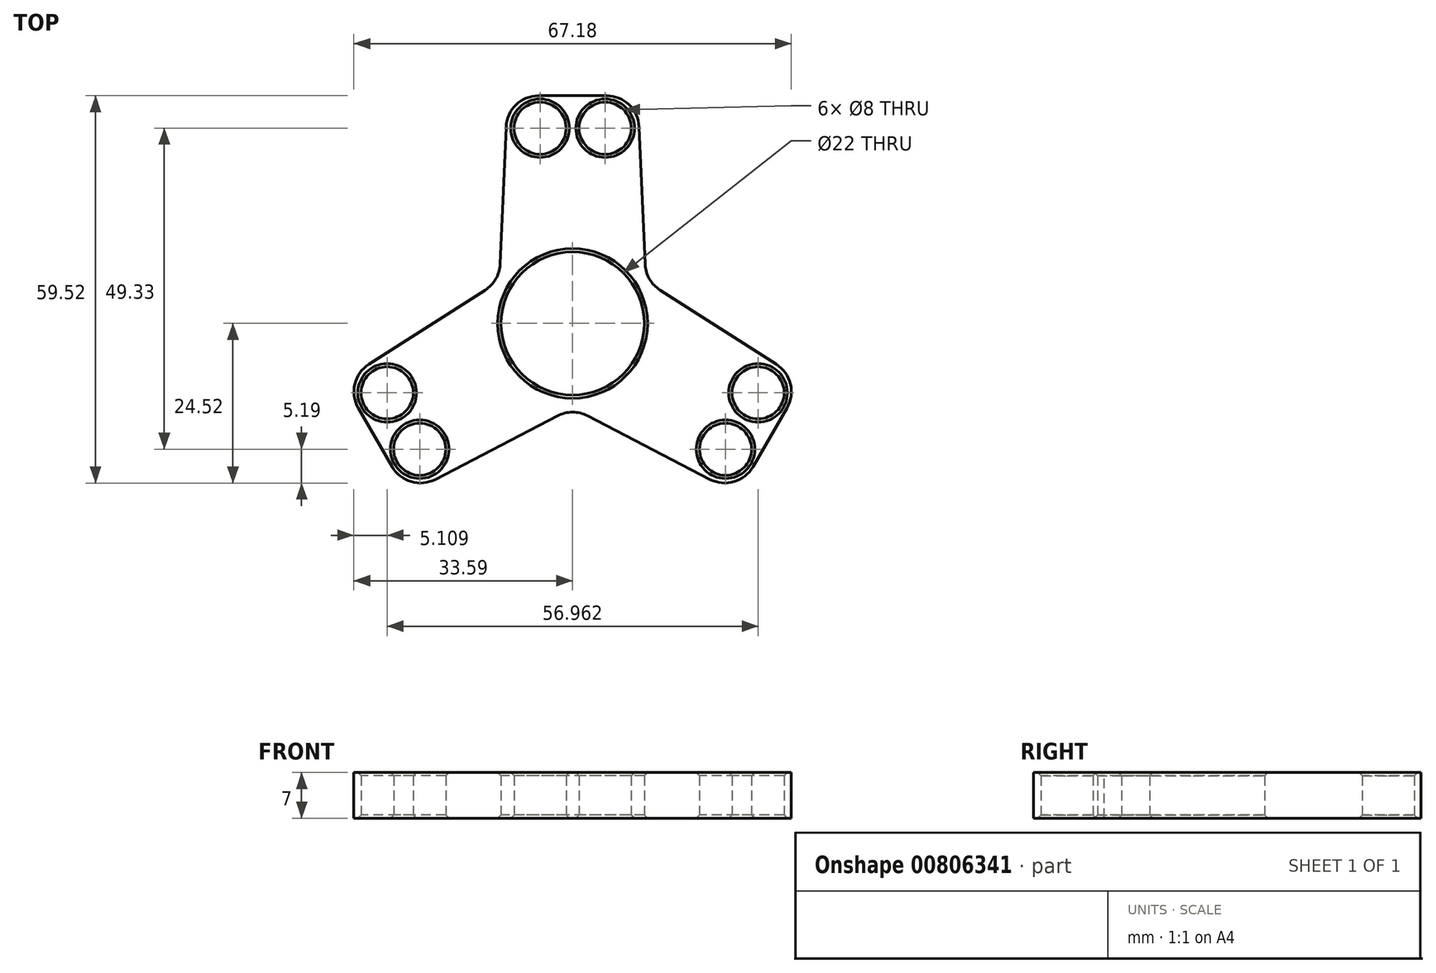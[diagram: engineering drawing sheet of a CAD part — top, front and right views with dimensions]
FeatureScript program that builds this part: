
annotation { "Feature Type Name" : "Feature", "Feature Type Description" : "" }
export const myFeature = defineFeature(function(context is Context, id is Id, definition is map)
    precondition{}
    {
        {
            var Q0;
            Q0=qCreatedBy(makeId("Top.planeOp"),FACE);
            var sketch = newSketch(context, id + "F0", { "sketchPlane" : qUnion([Q0])});
            skCircle(sketch, "E0", {"center": v(0, 0) * mm, "radius": 11 * mm});
            skCircle(sketch, "E1", {"center": v(0, 0) * mm, "radius": 13 * mm});
            skCircle(sketch, "E2", {"center": v(-5, 30) * mm, "radius": 4 * mm});
            skCircle(sketch, "E3.MirrorC", {"center": v(5, 30) * mm, "radius": 4 * mm});
            skCircle(sketch, "E4.1.0", {"center": v(-23.48, -19.33) * mm, "radius": 4 * mm});
            skCircle(sketch, "E4.1.1", {"center": v(-28.48, -10.67) * mm, "radius": 4 * mm});
            skCircle(sketch, "E4.2.0", {"center": v(28.48, -10.67) * mm, "radius": 4 * mm});
            skCircle(sketch, "E4.2.1", {"center": v(23.48, -19.33) * mm, "radius": 4 * mm});
            skLineSegment(sketch, "E5", {"start": v(0, 0) * mm, "end": v(-40.63, 23.46) * mm, "construction": true});
            skLineSegment(sketch, "E6", {"start": v(0, 0) * mm, "end": v(38.82, 22.41) * mm, "construction": true});
            skLineSegment(sketch, "E7", {"start": v(-11.26, 6.5) * mm, "end": v(-10, 35) * mm});
            skLineSegment(sketch, "E8", {"start": v(-10, 35) * mm, "end": v(10, 35) * mm});
            skLineSegment(sketch, "E9", {"start": v(10, 35) * mm, "end": v(11.26, 6.5) * mm});
            skLineSegment(sketch, "E10.1.0", {"start": v(0, -13) * mm, "end": v(-25.31, -26.16) * mm});
            skLineSegment(sketch, "E10.1.1", {"start": v(-25.31, -26.16) * mm, "end": v(-35.31, -8.84) * mm});
            skLineSegment(sketch, "E10.1.2", {"start": v(-35.31, -8.84) * mm, "end": v(-11.26, 6.5) * mm});
            skLineSegment(sketch, "E10.2.0", {"start": v(11.26, 6.5) * mm, "end": v(35.31, -8.84) * mm});
            skLineSegment(sketch, "E10.2.1", {"start": v(35.31, -8.84) * mm, "end": v(25.31, -26.16) * mm});
            skLineSegment(sketch, "E10.2.2", {"start": v(25.31, -26.16) * mm, "end": v(0, -13) * mm});
            skSolve(sketch);
        }
        {
            var Q0;
            Q0=makeQuery(id+"F0.imprint","IMPRINT",FACE,{"disambiguationData":[TD([[makeQuery(id+"F0.imprint","IMPRINT",EDGE,{"derivedFrom":sQuery(id+"F0.wireOp",EDGE,"E2")}),-1.0]])]});
            var Q1;
            Q1=makeQuery(id+"F0.imprint","IMPRINT",FACE,{"disambiguationData":[TD([[makeQuery(id+"F0.imprint","IMPRINT",EDGE,{"derivedFrom":sQuery(id+"F0.wireOp",EDGE,"E0")}),-1.0]])]});
            var Q2;
            Q2=makeQuery(id+"F0.imprint","IMPRINT",FACE,{"disambiguationData":[TD([[makeQuery(id+"F0.imprint","IMPRINT",EDGE,{"derivedFrom":sQuery(id+"F0.wireOp",EDGE,"E4.1.0")}),-1.0]])]});
            var Q3;
            Q3=makeQuery(id+"F0.imprint","IMPRINT",FACE,{"disambiguationData":[TD([[makeQuery(id+"F0.imprint","IMPRINT",EDGE,{"derivedFrom":sQuery(id+"F0.wireOp",EDGE,"E4.2.0")}),-1.0]])]});
            extrude(context, id + "F1", {"entities" : qUnion([Q0, Q1, Q2, Q3]), "endBound" : BoundingType.SYMMETRIC, "depth" : 7 * mm, "offsetDistance" : 25 * mm});
        }
        {
            var Q0;
            Q0=makeQuery(id+"F1.opExtrude","CAP_EDGE",EDGE,{"disambiguationData":[OSD([sQuery(id+"F0.wireOp",EDGE,"E2")])],"isStart":false});
            var Q1;
            Q1=makeQuery(id+"F1.opExtrude","CAP_EDGE",EDGE,{"disambiguationData":[OSD([sQuery(id+"F0.wireOp",EDGE,"E3.MirrorC")])],"isStart":false});
            var Q2;
            Q2=makeQuery(id+"F1.opExtrude","CAP_EDGE",EDGE,{"disambiguationData":[OSD([sQuery(id+"F0.wireOp",EDGE,"E0")])],"isStart":false});
            var Q3;
            Q3=makeQuery(id+"F1.opExtrude","CAP_EDGE",EDGE,{"disambiguationData":[OSD([sQuery(id+"F0.wireOp",EDGE,"E4.1.1")])],"isStart":false});
            var Q4;
            Q4=makeQuery(id+"F1.opExtrude","CAP_EDGE",EDGE,{"disambiguationData":[OSD([sQuery(id+"F0.wireOp",EDGE,"E4.1.0")])],"isStart":false});
            var Q5;
            Q5=makeQuery(id+"F1.opExtrude","CAP_EDGE",EDGE,{"disambiguationData":[OSD([sQuery(id+"F0.wireOp",EDGE,"E4.2.0")])],"isStart":false});
            var Q6;
            Q6=makeQuery(id+"F1.opExtrude","CAP_EDGE",EDGE,{"disambiguationData":[OSD([sQuery(id+"F0.wireOp",EDGE,"E4.2.1")])],"isStart":false});
            var Q7;
            Q7=makeQuery(id+"F1.opExtrude","CAP_EDGE",EDGE,{"disambiguationData":[OSD([sQuery(id+"F0.wireOp",EDGE,"E0")])],"isStart":true});
            var Q8;
            Q8=makeQuery(id+"F1.opExtrude","CAP_EDGE",EDGE,{"disambiguationData":[OSD([sQuery(id+"F0.wireOp",EDGE,"E4.1.0")])],"isStart":true});
            var Q9;
            Q9=makeQuery(id+"F1.opExtrude","CAP_EDGE",EDGE,{"disambiguationData":[OSD([sQuery(id+"F0.wireOp",EDGE,"E4.1.1")])],"isStart":true});
            var Q10;
            Q10=makeQuery(id+"F1.opExtrude","CAP_EDGE",EDGE,{"disambiguationData":[OSD([sQuery(id+"F0.wireOp",EDGE,"E4.2.1")])],"isStart":true});
            var Q11;
            Q11=makeQuery(id+"F1.opExtrude","CAP_EDGE",EDGE,{"disambiguationData":[OSD([sQuery(id+"F0.wireOp",EDGE,"E4.2.0")])],"isStart":true});
            var Q12;
            Q12=makeQuery(id+"F1.opExtrude","CAP_EDGE",EDGE,{"disambiguationData":[OSD([sQuery(id+"F0.wireOp",EDGE,"E3.MirrorC")])],"isStart":true});
            var Q13;
            Q13=makeQuery(id+"F1.opExtrude","CAP_EDGE",EDGE,{"disambiguationData":[OSD([sQuery(id+"F0.wireOp",EDGE,"E2")])],"isStart":true});
            chamfer(context, id + "F2", {"entities" : qUnion([Q0, Q1, Q2, Q3, Q4, Q5, Q6, Q7, Q8, Q9, Q10, Q11, Q12, Q13]), "width" : 0.5 * mm, "tangentPropagation" : true});
        }
        {
            var Q0;
            Q0=makeQuery(id+"F1.opExtrude","SWEPT_EDGE",EDGE,{"disambiguationData":[OSD([sQuery(id+"F0.wireOp",EDGE,"E10.1.0"),sQuery(id+"F0.wireOp",EDGE,"E10.1.1")])]});
            var Q1;
            Q1=makeQuery(id+"F1.opExtrude","SWEPT_EDGE",EDGE,{"disambiguationData":[OSD([sQuery(id+"F0.wireOp",EDGE,"E10.1.1"),sQuery(id+"F0.wireOp",EDGE,"E10.1.2")])]});
            var Q2;
            Q2=makeQuery(id+"F1.opExtrude","SWEPT_EDGE",EDGE,{"disambiguationData":[OSD([sQuery(id+"F0.wireOp",EDGE,"E10.2.1"),sQuery(id+"F0.wireOp",EDGE,"E10.2.2")])]});
            var Q3;
            Q3=makeQuery(id+"F1.opExtrude","SWEPT_EDGE",EDGE,{"disambiguationData":[OSD([sQuery(id+"F0.wireOp",EDGE,"E10.2.0"),sQuery(id+"F0.wireOp",EDGE,"E10.2.1")])]});
            var Q4;
            Q4=makeQuery(id+"F1.opExtrude","SWEPT_EDGE",EDGE,{"disambiguationData":[OSD([sQuery(id+"F0.wireOp",EDGE,"E8"),sQuery(id+"F0.wireOp",EDGE,"E9")])]});
            var Q5;
            Q5=makeQuery(id+"F1.opExtrude","SWEPT_EDGE",EDGE,{"disambiguationData":[OSD([sQuery(id+"F0.wireOp",EDGE,"E7"),sQuery(id+"F0.wireOp",EDGE,"E8")])]});
            var Q6;
            Q6=makeQuery(id+"F1.opExtrude","SWEPT_EDGE",EDGE,{"disambiguationData":[OSD([sQuery(id+"F0.wireOp",EDGE,"E1"),sQuery(id+"F0.wireOp",EDGE,"E7"),sQuery(id+"F0.wireOp",EDGE,"E10.1.2")])]});
            var Q7;
            Q7=makeQuery(id+"F1.opExtrude","SWEPT_EDGE",EDGE,{"disambiguationData":[OSD([sQuery(id+"F0.wireOp",EDGE,"E1"),sQuery(id+"F0.wireOp",EDGE,"E9"),sQuery(id+"F0.wireOp",EDGE,"E10.2.0")])]});
            var Q8;
            Q8=makeQuery(id+"F1.opExtrude","SWEPT_EDGE",EDGE,{"disambiguationData":[OSD([sQuery(id+"F0.wireOp",EDGE,"E1"),sQuery(id+"F0.wireOp",EDGE,"E10.1.0"),sQuery(id+"F0.wireOp",EDGE,"E10.2.2")])]});
            fillet(context, id + "F3", {"entities" : qUnion([Q0, Q1, Q2, Q3, Q4, Q5, Q6, Q7, Q8]), "radius" : 5 * mm, "tangentPropagation" : true, "allowEdgeOverflow" : false});
        }
    });
